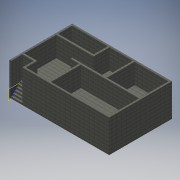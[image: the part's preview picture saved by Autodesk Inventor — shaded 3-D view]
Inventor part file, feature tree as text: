
AUTODESK INVENTOR PART (.ipt)
format: ipt  version: 2017 (Build 210142000, 142)  size: 270,848 bytes
history: native  units: mm
features: extrude x4, sketch x4, projected_geometry x3, plane x1
ambient origin geometry x8: Origin, YZ Plane, XZ Plane, XY Plane, X Axis, Y Axis, Z Axis, Center Point
bodies: Volumenkörper1 (feature_tree)
feature tree (12):
  extrude  "Extrusion1"  Depth=7150.0mm
  plane  "Arbeitsebene1"
  extrude  "Extrusion3"  [1 undecoded]
  extrude  "Extrusion4"  Depth=200.0mm
  extrude  "Extrusion5"  Depth=200.0mm
  sketch  "Skizze1"  dims[d0=11360.0mm d1=7150.0mm]
  sketch  "Skizze2"  dims[d2=1400.0mm d3=0.0mm d4=-200.0mm]
  projected_geometry  "Projizierte Kontur1"
  sketch  "Skizze4"  dims[d5=200.0mm d6=200.0mm]
  projected_geometry  "Projizierte Kontur3"
  sketch  "Skizze5"  dims[d7=200.0mm d8=200.0mm d9=200.0mm d10=200.0mm d11=200.0mm d12=200.0mm d15=200.0mm d16=200.0mm d17=200.0mm d18=200.0mm d19=1280.0mm d20=0.0mm d41=200.0mm d42=200.0mm d43=200.0mm d44=200.0mm d45=200.0mm d46=1300.0mm d47=2300.0mm d48=0.0mm d49=200.0mm d50=200.0mm d51=6620.0mm d52=3400.0mm d53=970.0mm d54=1600.0mm d55=200.0mm d56=4050.0mm d57=200.0mm d58=2300.0mm d59=0.0mm d60=3850.0mm d61=200.0mm]
  projected_geometry  "Projizierte Kontur4"
note: 1 required parameter value undecoded (feature->parameter linkage not recoverable at this tier; creation-order binding heuristic only, values carry confidence <= 0.55)
